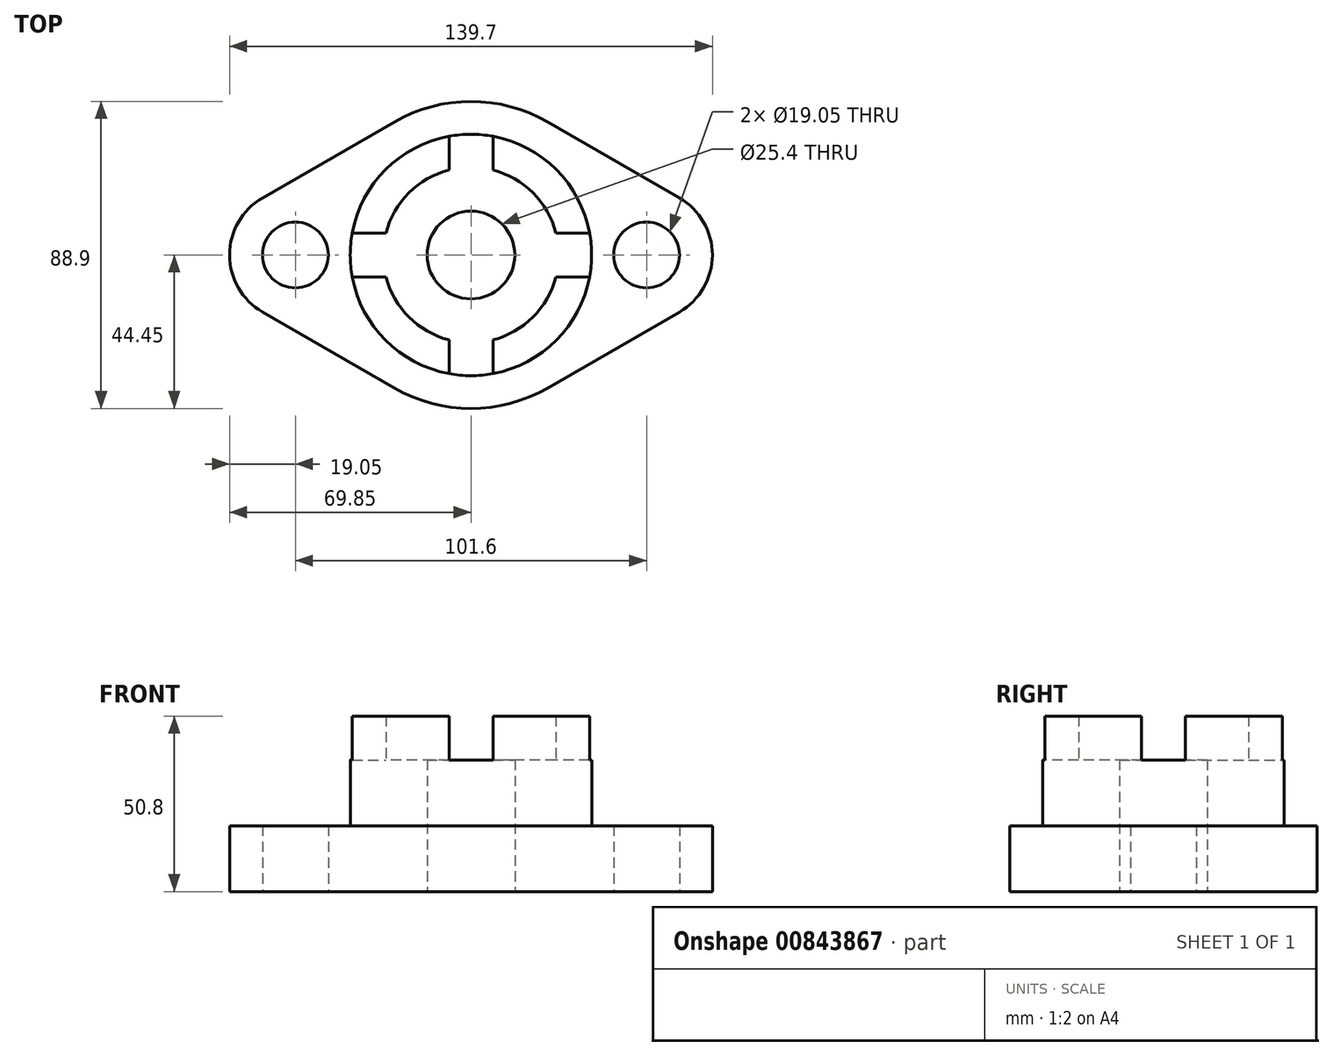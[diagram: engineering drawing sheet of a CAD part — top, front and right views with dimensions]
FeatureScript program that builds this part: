
annotation { "Feature Type Name" : "Feature", "Feature Type Description" : "" }
export const myFeature = defineFeature(function(context is Context, id is Id, definition is map)
    precondition{}
    {
        {
            var Q0;
            Q0=qCreatedBy(makeId("Top.planeOp"),FACE);
            var sketch = newSketch(context, id + "F0", { "sketchPlane" : qUnion([Q0])});
            skCircle(sketch, "E0", {"center": v(0, 0) * mm, "radius": 12.7 * mm});
            skCircle(sketch, "E1", {"center": v(0, 0) * mm, "radius": 25.4 * mm});
            skCircle(sketch, "E2", {"center": v(0, 0) * mm, "radius": 34.93 * mm});
            skCircle(sketch, "E3", {"center": v(-50.8, 0) * mm, "radius": 9.53 * mm});
            skCircle(sketch, "E4", {"center": v(50.8, 0) * mm, "radius": 9.53 * mm});
            skArc(sketch, "E5", {"start": v(-22.23, -38.5) * mm, "mid": v(0, -44.45) * mm, "end": v(22.23, -38.5) * mm});
            skArc(sketch, "E6", {"start": v(-60.32, 16.5) * mm, "mid": v(-69.85, 0) * mm, "end": v(-60.32, -16.5) * mm});
            skArc(sketch, "E7", {"start": v(60.33, -16.5) * mm, "mid": v(69.85, 0) * mm, "end": v(60.32, 16.5) * mm});
            skArc(sketch, "E8.trimOffspring", {"start": v(22.23, 38.5) * mm, "mid": v(0, 44.45) * mm, "end": v(-22.23, 38.5) * mm});
            skLineSegment(sketch, "E9", {"start": v(60.32, 16.5) * mm, "end": v(22.23, 38.5) * mm});
            skLineSegment(sketch, "E10", {"start": v(-60.32, 16.5) * mm, "end": v(-22.23, 38.5) * mm});
            skLineSegment(sketch, "E11", {"start": v(-60.32, -16.5) * mm, "end": v(-22.23, -38.5) * mm});
            skLineSegment(sketch, "E12", {"start": v(60.33, -16.5) * mm, "end": v(22.22, -38.5) * mm});
            skLineSegment(sketch, "E13", {"start": v(0, 0) * mm, "end": v(0, -12.7) * mm});
            skLineSegment(sketch, "E14", {"start": v(6.35, -29.9) * mm, "end": v(6.35, -34.34) * mm});
            skLineSegment(sketch, "E15", {"start": v(6.35, -34.34) * mm, "end": v(6.35, -24.6) * mm});
            skLineSegment(sketch, "E16", {"start": v(-6.35, -24.6) * mm, "end": v(-6.35, -34.34) * mm});
            skLineSegment(sketch, "E17", {"start": v(0, 0) * mm, "end": v(-12.7, 0) * mm});
            skLineSegment(sketch, "E18", {"start": v(-30.57, 6.35) * mm, "end": v(-24.6, 6.35) * mm});
            skLineSegment(sketch, "E19", {"start": v(-24.6, -6.35) * mm, "end": v(-34.34, -6.35) * mm});
            skLineSegment(sketch, "E20", {"start": v(-34.34, 6.35) * mm, "end": v(-30.57, 6.35) * mm});
            skLineSegment(sketch, "E21", {"start": v(0, 0) * mm, "end": v(0, 12.7) * mm});
            skLineSegment(sketch, "E22", {"start": v(6.35, 25.4) * mm, "end": v(6.35, 34.34) * mm});
            skLineSegment(sketch, "E23", {"start": v(-6.35, 34.34) * mm, "end": v(-6.35, 24.6) * mm});
            skLineSegment(sketch, "E24", {"start": v(6.35, 24.6) * mm, "end": v(6.35, 25.4) * mm});
            skLineSegment(sketch, "E25", {"start": v(0, 0) * mm, "end": v(25.4, 0) * mm});
            skLineSegment(sketch, "E26", {"start": v(25.4, -6.35) * mm, "end": v(34.34, -6.35) * mm});
            skLineSegment(sketch, "E27", {"start": v(34.34, 6.35) * mm, "end": v(24.6, 6.35) * mm});
            skLineSegment(sketch, "E28", {"start": v(24.6, -6.35) * mm, "end": v(25.4, -6.35) * mm});
            skSolve(sketch);
        }
        {
            var Q0;
            Q0 = qSketchRegion(id + "F0", true);
            extrude(context, id + "F1", {"entities" : qUnion([Q0]), "depth" : 19.05 * mm, "offsetDistance" : 25.4 * mm});
        }
        {
            var Q0;
            {var subQ1=sQuery(id+"F0.wireOp",EDGE,"E18");Q0=makeQuery(id+"F0.imprint","IMPRINT",FACE,{"disambiguationData":[TD([[makeQuery(id+"F0.imprint","IMPRINT",EDGE,{"derivedFrom":subQ1}),1.0]])]});}
            var Q1;
            {var subQ0=sQuery(id+"F0.wireOp",EDGE,"E16");Q1=makeQuery(id+"F0.imprint","IMPRINT",FACE,{"disambiguationData":[TD([[makeQuery(id+"F0.imprint","IMPRINT",EDGE,{"derivedFrom":subQ0}),-1.0]])]});}
            var Q2;
            {var subQ5=sQuery(id+"F0.wireOp",EDGE,"E26");Q2=makeQuery(id+"F0.imprint","IMPRINT",FACE,{"disambiguationData":[TD([[makeQuery(id+"F0.imprint","IMPRINT",EDGE,{"derivedFrom":subQ5}),-1.0]])]});}
            var Q3;
            {var subQ1=sQuery(id+"F0.wireOp",EDGE,"E22");Q3=makeQuery(id+"F0.imprint","IMPRINT",FACE,{"disambiguationData":[TD([[makeQuery(id+"F0.imprint","IMPRINT",EDGE,{"derivedFrom":subQ1}),-1.0]])]});}
            extrude(context, id + "F2", {"entities" : qUnion([Q0, Q1, Q2, Q3]), "operationType" : NewBodyOperationType.ADD, "depth" : 50.8 * mm, "offsetDistance" : 25.4 * mm});
        }
        {
            var Q0;
            {var subQ0=sQuery(id+"F0.wireOp",EDGE,"E1");var subQ7=makeQuery(id+"F0.imprint","IMPRINT",VERTEX,{"derivedFrom":subQ0});Q0=makeQuery(id+"F0.imprint","IMPRINT",FACE,{"disambiguationData":[TD([[makeQuery(id+"F0.imprint","IMPRINT",EDGE,{"disambiguationData":[TD([[subQ7,-1.0]])],"derivedFrom":subQ0}),1.0]])]});}
            var Q1;
            {var subQ6=sQuery(id+"F0.wireOp",EDGE,"E16");Q1=makeQuery(id+"F0.imprint","IMPRINT",FACE,{"disambiguationData":[TD([[makeQuery(id+"F0.imprint","IMPRINT",EDGE,{"derivedFrom":subQ6}),1.0]])]});}
            var Q2;
            {var subQ1=sQuery(id+"F0.wireOp",EDGE,"E18");Q2=makeQuery(id+"F0.imprint","IMPRINT",FACE,{"disambiguationData":[TD([[makeQuery(id+"F0.imprint","IMPRINT",EDGE,{"derivedFrom":subQ1}),-1.0]])]});}
            var Q3;
            {var subQ0=sQuery(id+"F0.wireOp",EDGE,"E22");Q3=makeQuery(id+"F0.imprint","IMPRINT",FACE,{"disambiguationData":[TD([[makeQuery(id+"F0.imprint","IMPRINT",EDGE,{"derivedFrom":subQ0}),1.0]])]});}
            var Q4;
            {var subQ0=sQuery(id+"F0.wireOp",EDGE,"E26");Q4=makeQuery(id+"F0.imprint","IMPRINT",FACE,{"disambiguationData":[TD([[makeQuery(id+"F0.imprint","IMPRINT",EDGE,{"derivedFrom":subQ0}),1.0]])]});}
            extrude(context, id + "F3", {"entities" : qUnion([Q0, Q1, Q2, Q3, Q4]), "operationType" : NewBodyOperationType.ADD, "depth" : 38.1 * mm, "offsetDistance" : 25.4 * mm});
        }
    });
